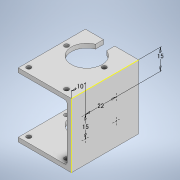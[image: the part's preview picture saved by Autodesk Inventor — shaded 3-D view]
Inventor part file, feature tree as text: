
AUTODESK INVENTOR PART (.ipt)
format: ipt  version: 2022 (Build 260153000, 153)  size: 194,048 bytes
history: native  units: mm
features: sketch x7, extrude x3, hole x3, other x1, fillet x1
ambient origin geometry x8: Origin, YZ Plane, XZ Plane, XY Plane, X Axis, Y Axis, Z Axis, Center Point
bodies: Body1 (feature_tree)
feature tree (15):
  other  "ソリッド1"
  extrude  "押し出し1"  Depth=48.0mm
  extrude  "押し出し2"  Depth=38.0mm
  hole  "穴1"  [1 undecoded]
  hole  "穴2"  [1 undecoded]
  sketch  "スケッチ6"
  fillet  "フィレット1"  Radius=3.0mm
  extrude  "押し出し3"  Depth=3.0mm
  hole  "穴5"  [1 undecoded]
  sketch  "スケッチ1"
  sketch  "スケッチ2"
  sketch  "スケッチ3"
  sketch  "スケッチ4"
  sketch  "スケッチ7"
  sketch  "スケッチ8"
note: 3 required parameter values undecoded (feature->parameter linkage not recoverable at this tier; creation-order binding heuristic only, values carry confidence <= 0.55)
